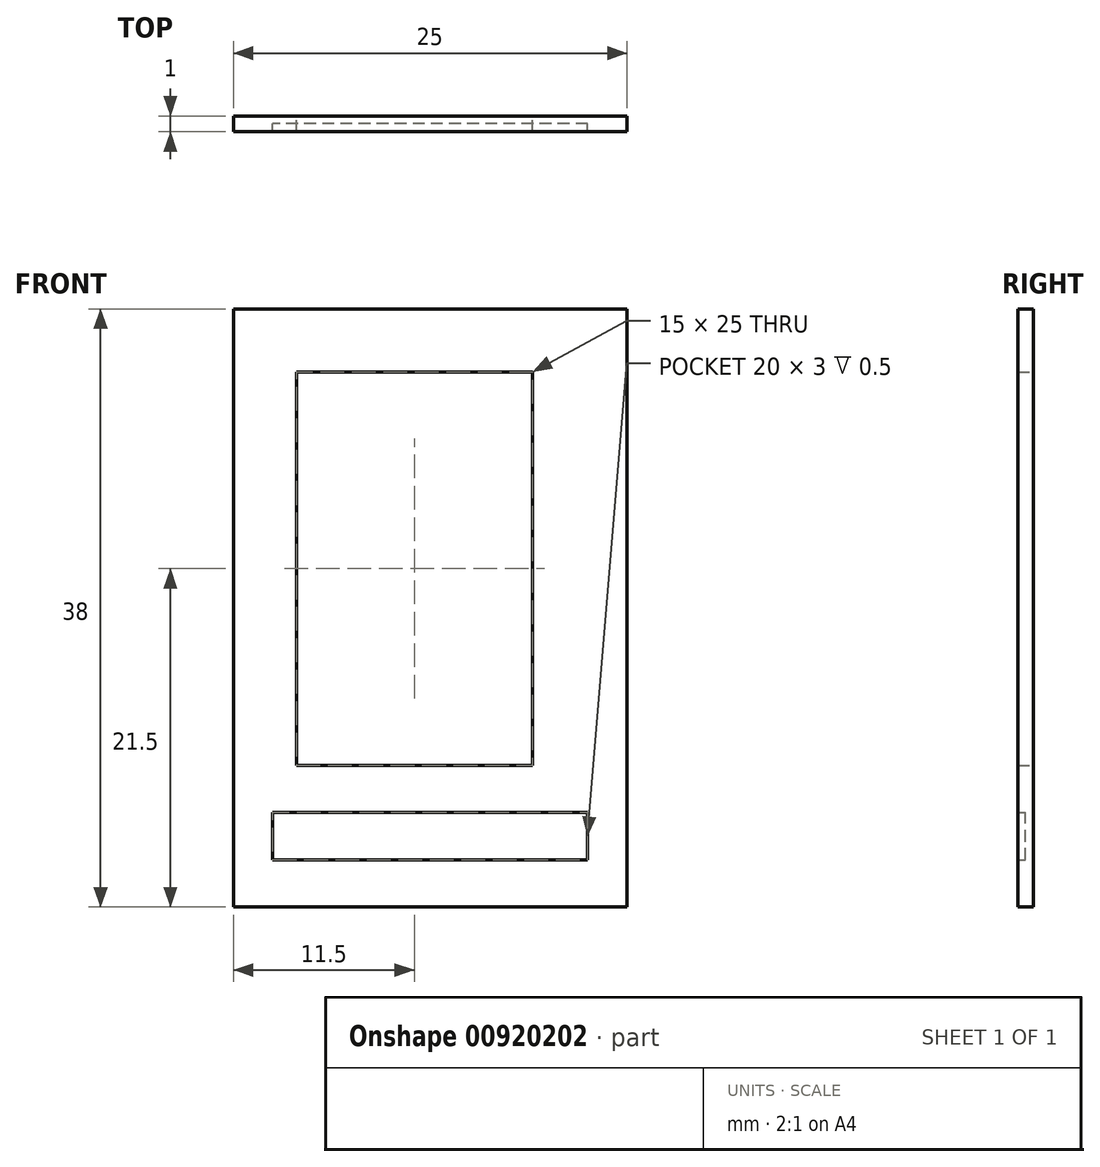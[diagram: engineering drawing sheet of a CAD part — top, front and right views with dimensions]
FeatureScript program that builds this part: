
annotation { "Feature Type Name" : "Feature", "Feature Type Description" : "" }
export const myFeature = defineFeature(function(context is Context, id is Id, definition is map)
    precondition{}
    {
        {
            var Q0;
            Q0=qCreatedBy(makeId("Front.planeOp"),FACE);
            var sketch = newSketch(context, id + "F0", { "sketchPlane" : qUnion([Q0])});
            skLineSegment(sketch, "E0.bottom", {"start": v(12.5, -19) * mm, "end": v(-12.5, -19) * mm});
            skLineSegment(sketch, "E0.top", {"start": v(12.5, 19) * mm, "end": v(-12.5, 19) * mm});
            skLineSegment(sketch, "E0.left", {"start": v(12.5, -19) * mm, "end": v(12.5, 19) * mm});
            skLineSegment(sketch, "E0.right", {"start": v(-12.5, -19) * mm, "end": v(-12.5, 19) * mm});
            skPoint(sketch, "E0.middle", {"position": v(0, 0) * mm});
            skLineSegment(sketch, "E1.bottom", {"start": v(-8.5, 15) * mm, "end": v(6.5, 15) * mm});
            skLineSegment(sketch, "E1.top", {"start": v(-8.5, -10) * mm, "end": v(6.5, -10) * mm});
            skLineSegment(sketch, "E1.left", {"start": v(-8.5, 15) * mm, "end": v(-8.5, -10) * mm});
            skLineSegment(sketch, "E1.right", {"start": v(6.5, 15) * mm, "end": v(6.5, -10) * mm});
            skLineSegment(sketch, "E2.bottom", {"start": v(-10, -13) * mm, "end": v(10, -13) * mm});
            skLineSegment(sketch, "E2.top", {"start": v(-10, -16) * mm, "end": v(10, -16) * mm});
            skLineSegment(sketch, "E2.left", {"start": v(-10, -13) * mm, "end": v(-10, -16) * mm});
            skLineSegment(sketch, "E2.right", {"start": v(10, -13) * mm, "end": v(10, -16) * mm});
            skSolve(sketch);
        }
        {
            var Q0;
            Q0=makeQuery(id+"F0.imprint","IMPRINT",FACE,{"disambiguationData":[TD([[makeQuery(id+"F0.imprint","IMPRINT",EDGE,{"derivedFrom":sQuery(id+"F0.wireOp",EDGE,"E0.bottom")}),-1.0]])]});
            extrude(context, id + "F1", {"entities" : qUnion([Q0]), "depth" : 1 * mm, "offsetDistance" : 25 * mm});
        }
        {
            var Q0;
            Q0=makeQuery(id+"F1.opExtrude","CAP_FACE",FACE,{"disambiguationData":[OSD([sQuery(id+"F0.wireOp",EDGE,"E0.bottom"),sQuery(id+"F0.wireOp",EDGE,"E0.top"),sQuery(id+"F0.wireOp",EDGE,"E0.left"),sQuery(id+"F0.wireOp",EDGE,"E0.right"),sQuery(id+"F0.wireOp",EDGE,"E1.bottom"),sQuery(id+"F0.wireOp",EDGE,"E1.top"),sQuery(id+"F0.wireOp",EDGE,"E1.left"),sQuery(id+"F0.wireOp",EDGE,"E1.right"),sQuery(id+"F0.wireOp",EDGE,"E2.bottom"),sQuery(id+"F0.wireOp",EDGE,"E2.top"),sQuery(id+"F0.wireOp",EDGE,"E2.left"),sQuery(id+"F0.wireOp",EDGE,"E2.right")])],"isStart":true});
            var sketch = newSketch(context, id + "F2", { "sketchPlane" : qUnion([Q0])});
            skLineSegment(sketch, "E3.bottom", {"start": v(-11.2, -11.97) * mm, "end": v(11.3, -11.97) * mm});
            skLineSegment(sketch, "E3.top", {"start": v(-11.2, -16.78) * mm, "end": v(11.3, -16.78) * mm});
            skLineSegment(sketch, "E3.left", {"start": v(-11.2, -11.97) * mm, "end": v(-11.2, -16.78) * mm});
            skLineSegment(sketch, "E3.right", {"start": v(11.3, -11.97) * mm, "end": v(11.3, -16.78) * mm});
            skSolve(sketch);
        }
        {
            var Q0;
            Q0=makeQuery(id+"F2.imprint","IMPRINT",FACE,{"disambiguationData":[TD([[makeQuery(id+"F2.imprint","IMPRINT",EDGE,{"derivedFrom":sQuery(id+"F2.wireOp",EDGE,"E3.bottom")}),-1.0]])]});
            var Q1;
            Q1=makeQuery(id+"F2.imprint","IMPRINT",FACE,{"disambiguationData":[TD([[makeQuery(id+"F2.imprint","IMPRINT",EDGE,{"derivedFrom":makeQuery(id+"F1.opExtrude","CAP_EDGE",EDGE,{"disambiguationData":[OSD([sQuery(id+"F0.wireOp",EDGE,"E2.bottom")])],"isStart":true})}),1.0]])]});
            extrude(context, id + "F3", {"entities" : qUnion([Q0, Q1]), "operationType" : NewBodyOperationType.ADD, "oppositeDirection" : true, "depth" : 0.5 * mm, "offsetDistance" : 25 * mm});
        }
    });
